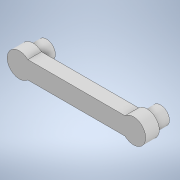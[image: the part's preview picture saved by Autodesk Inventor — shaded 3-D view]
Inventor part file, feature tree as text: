
AUTODESK INVENTOR PART (.ipt)
format: ipt  version: 2022 (Build 260153000, 153)  size: 123,392 bytes
history: native  units: in
note: dims shown in document units (in); Inventor stores cm internally (conversion verified against a paired STEP export)
features: extrude x2, sketch x1
ambient origin geometry x8: Origin, YZ Plane, XZ Plane, XY Plane, X Axis, Y Axis, Z Axis, Center Point
bodies: Body1 (feature_tree)
feature tree (3):
  sketch  "Sketch2"  dims[d0=0.1969in d1=0.0in d2=0.1969in d3=0.0in d4=0.2559in d6=0.3543in d7=0.2559in d8=1.6535in]
  extrude  "Extrusion1"  Depth=0.1969in TaperAngle=0.0deg
  extrude  "Extrusion2"  Depth=0.2559in
